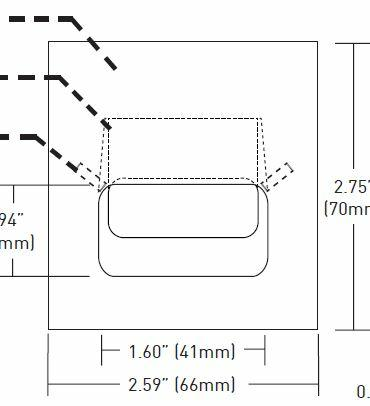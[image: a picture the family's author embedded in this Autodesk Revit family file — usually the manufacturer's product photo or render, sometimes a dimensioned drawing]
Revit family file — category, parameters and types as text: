
# Revit family: Lighting-Steplight-Lucifer-ISL2
name_source: partatom
category: Lighting Fixtures
revit_build: Autodesk Revit 2016 (Build: 20170117_1200(x64)
units: mm (PartAtom-declared; Revit-internal decimal feet)

## family parameters
Cut with Voids When Loaded = No
Host = Face
Light Source = Yes
Part Type = Normal
Room Calculation Point = No
Round Connector Dimension = Use Diameter
Shared = No

## types (1)
- Lighting-Steplight-Lucifer-ISL2
    Apparent Load = 0 VA
    Color Filter = 16777215
    Default Elevation = 4' - 0"
    Description = Steplight
    Dimming Lamp Color Temperature Shift = <None>
    Emit Shape Visible in Rendering = No
    Emit from Rectangle Length = 0' - 3 9/32"
    Emit from Rectangle Width = 0' - 1 11/16"
    Lamp = LED
    Length = 0' - 4 9/32"
    Manufacturer = Lucifer Lighting
    Model = ISL2
    Number of Poles = 1
    Photometric Web File = Load File
    Power Factor = 1
    Tilt Angle = -90.00°
    URL = http://www.luciferlighting.com
    Voltage = 0 V
    Width = 0' - 4 9/32"

## geometry (parser evidence)
native form markers: Sweep x3
no freeform markers — native parametric forms only
